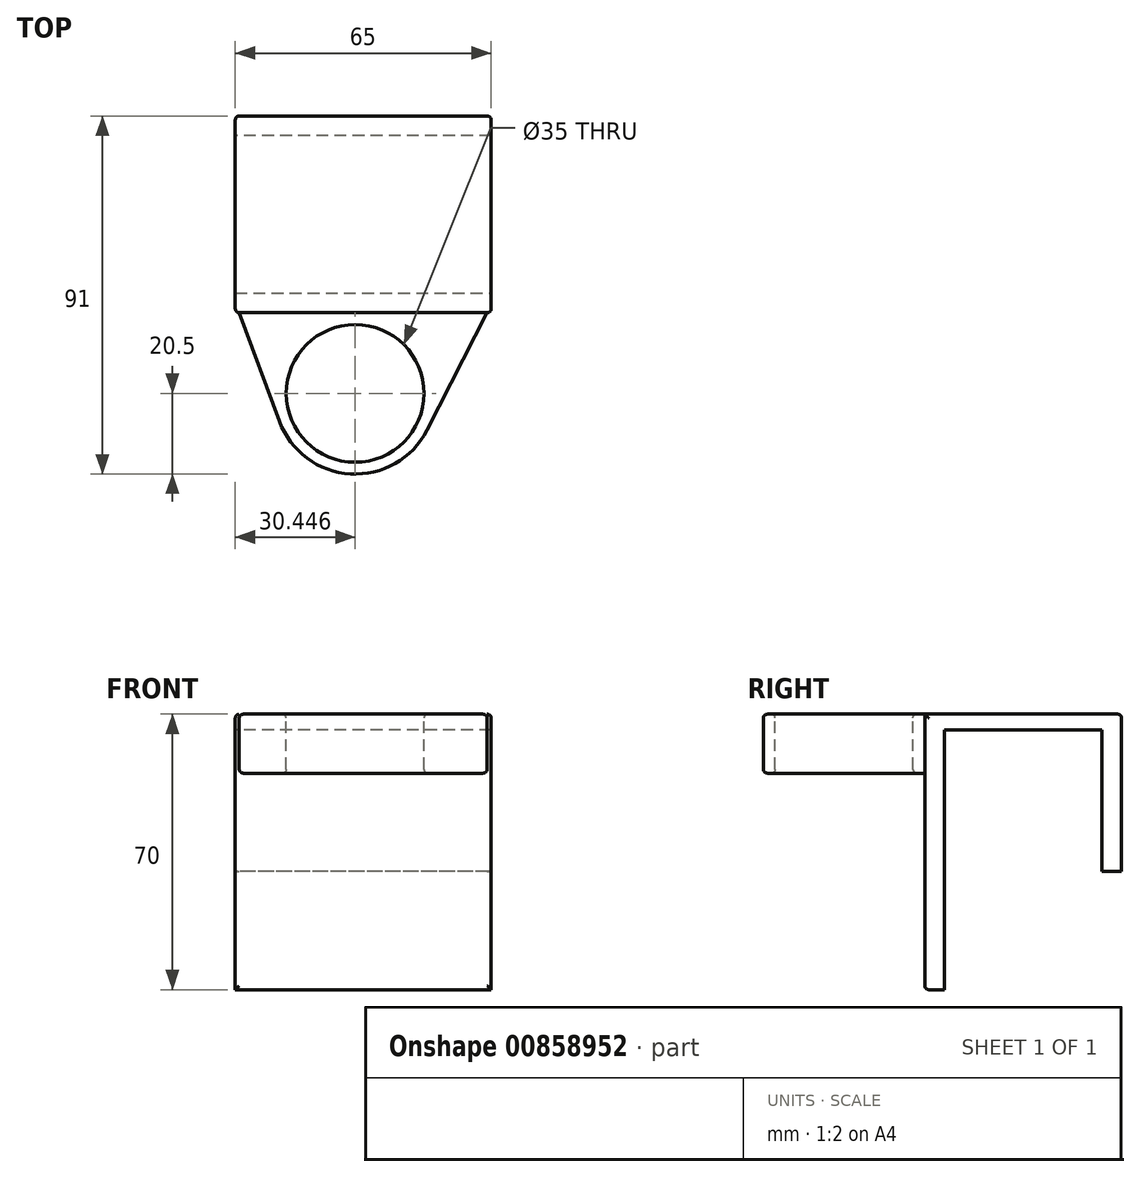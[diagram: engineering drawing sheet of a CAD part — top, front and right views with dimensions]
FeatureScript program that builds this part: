
annotation { "Feature Type Name" : "Feature", "Feature Type Description" : "" }
export const myFeature = defineFeature(function(context is Context, id is Id, definition is map)
    precondition{}
    {
        {
            var Q0;
            Q0=qCreatedBy(makeId("Front.planeOp"),FACE);
            var sketch = newSketch(context, id + "F0", { "sketchPlane" : qUnion([Q0])});
            skLineSegment(sketch, "E0.bottom", {"start": v(-49.34, 35.14) * mm, "end": v(15.66, 35.14) * mm});
            skLineSegment(sketch, "E0.top", {"start": v(-49.34, -34.86) * mm, "end": v(15.66, -34.86) * mm});
            skLineSegment(sketch, "E0.left", {"start": v(-49.34, 35.14) * mm, "end": v(-49.34, -34.86) * mm});
            skLineSegment(sketch, "E0.right", {"start": v(15.66, 35.14) * mm, "end": v(15.66, -34.86) * mm});
            skSolve(sketch);
        }
        {
            var Q0;
            Q0 = qSketchRegion(id + "F0", true);
            extrude(context, id + "F1", {"entities" : qUnion([Q0]), "oppositeDirection" : true, "depth" : 50 * mm, "offsetDistance" : 25.4 * mm});
        }
        {
            var Q0;
            Q0=makeQuery(id+"F1.opExtrude","SWEPT_FACE",FACE,{"disambiguationData":[OSD([sQuery(id+"F0.wireOp",EDGE,"E0.top")])]});
            var sketch = newSketch(context, id + "F2", { "sketchPlane" : qUnion([Q0])});
            skLineSegment(sketch, "E1.bottom", {"start": v(-49.34, -5) * mm, "end": v(15.66, -5) * mm});
            skLineSegment(sketch, "E1.top", {"start": v(-49.34, -45) * mm, "end": v(15.66, -45) * mm});
            skLineSegment(sketch, "E1.left", {"start": v(-49.34, -5) * mm, "end": v(-49.34, -45) * mm});
            skLineSegment(sketch, "E1.right", {"start": v(15.66, -5) * mm, "end": v(15.66, -45) * mm});
            skLineSegment(sketch, "E2.bottom", {"start": v(-16.84, 0) * mm, "end": v(-16.84, 0) * mm});
            skLineSegment(sketch, "E2.top", {"start": v(-16.84, -5) * mm, "end": v(-16.84, -5) * mm});
            skLineSegment(sketch, "E2.left", {"start": v(-16.84, 0) * mm, "end": v(-16.84, -5) * mm, "construction": true});
            skLineSegment(sketch, "E2.right", {"start": v(-16.84, 0) * mm, "end": v(-16.84, -5) * mm, "construction": true});
            skLineSegment(sketch, "E3.bottom", {"start": v(-16.84, -45) * mm, "end": v(-16.84, -45) * mm});
            skLineSegment(sketch, "E3.top", {"start": v(-16.84, -50) * mm, "end": v(-16.84, -50) * mm});
            skLineSegment(sketch, "E3.left", {"start": v(-16.84, -45) * mm, "end": v(-16.84, -50) * mm, "construction": true});
            skLineSegment(sketch, "E3.right", {"start": v(-16.84, -45) * mm, "end": v(-16.84, -50) * mm, "construction": true});
            skSolve(sketch);
        }
        {
            var Q0;
            Q0=makeQuery(id+"F2.imprint","IMPRINT",FACE,{"disambiguationData":[TD([[makeQuery(id+"F2.imprint","IMPRINT",EDGE,{"derivedFrom":sQuery(id+"F2.wireOp",EDGE,"E1.bottom")}),-1.0]])]});
            extrude(context, id + "F3", {"entities" : qUnion([Q0]), "operationType" : NewBodyOperationType.REMOVE, "endBound" : BoundingType.UP_TO_NEXT, "oppositeDirection" : true, "depth" : 25 * mm, "hasOffset" : true, "offsetDistance" : 4 * mm});
        }
        {
            var Q0;
            {var subQ2=sQuery(id+"F0.wireOp",EDGE,"E0.top");Q0=makeQuery(id+"F3.boolean.opBoolean","SPLIT",FACE,{"disambiguationData":[TD([makeQuery(id+"F3.opExtrude","SWEPT_FACE",FACE,{"disambiguationData":[OSD([sQuery(id+"F2.wireOp",EDGE,"E1.top")])]})])],"derivedFrom":makeQuery(id+"F1.opExtrude","SWEPT_FACE",FACE,{"disambiguationData":[OSD([subQ2])]})});}
            extrude(context, id + "F4", {"entities" : qUnion([Q0]), "operationType" : NewBodyOperationType.REMOVE, "endBound" : BoundingType.UP_TO_NEXT, "oppositeDirection" : true, "depth" : 25 * mm, "hasOffset" : true, "offsetDistance" : 40 * mm});
        }
        {
            var Q0;
            Q0=makeQuery(id+"F1.opExtrude","SWEPT_FACE",FACE,{"disambiguationData":[OSD([sQuery(id+"F0.wireOp",EDGE,"E0.bottom")])]});
            var sketch = newSketch(context, id + "F5", { "sketchPlane" : qUnion([Q0])});
            skCircle(sketch, "E4", {"center": v(-18.9, -20.5) * mm, "radius": 17.5 * mm});
            skCircle(sketch, "E5", {"center": v(-18.9, -20.5) * mm, "radius": 20.5 * mm});
            skLineSegment(sketch, "E6", {"start": v(-38.12, -27.61) * mm, "end": v(-48.34, 0) * mm});
            skLineSegment(sketch, "E7", {"start": v(14.66, 0) * mm, "end": v(-0.65, -29.86) * mm});
            skLineSegment(sketch, "E8", {"start": v(-48.34, 50) * mm, "end": v(-48.34, 0) * mm, "construction": true});
            skLineSegment(sketch, "E9", {"start": v(14.66, 50) * mm, "end": v(14.66, 0) * mm, "construction": true});
            skSolve(sketch);
        }
        {
            var Q0;
            Q0=makeQuery(id+"F5.imprint","IMPRINT",FACE,{"disambiguationData":[TD([[makeQuery(id+"F5.imprint","IMPRINT",EDGE,{"derivedFrom":sQuery(id+"F5.wireOp",EDGE,"E4")}),1.0]])]});
            extrude(context, id + "F6", {"entities" : qUnion([Q0]), "operationType" : NewBodyOperationType.REMOVE, "oppositeDirection" : true, "depth" : 25 * mm, "offsetDistance" : 25 * mm});
        }
        {
            var Q0;
            {var subQ0=sQuery(id+"F5.wireOp",EDGE,"E6");Q0=makeQuery(id+"F5.imprint","IMPRINT",FACE,{"disambiguationData":[TD([[makeQuery(id+"F5.imprint","IMPRINT",EDGE,{"derivedFrom":subQ0}),-1.0]])]});}
            var Q1;
            {var subQ0=sQuery(id+"F5.wireOp",EDGE,"E7");Q1=makeQuery(id+"F5.imprint","IMPRINT",FACE,{"disambiguationData":[TD([[makeQuery(id+"F5.imprint","IMPRINT",EDGE,{"derivedFrom":subQ0}),-1.0]])]});}
            var Q2;
            Q2=makeQuery(id+"F5.imprint","IMPRINT",FACE,{"disambiguationData":[TD([[makeQuery(id+"F5.imprint","IMPRINT",EDGE,{"derivedFrom":sQuery(id+"F5.wireOp",EDGE,"E4")}),-1.0]])]});
            extrude(context, id + "F7", {"entities" : qUnion([Q0, Q1, Q2]), "oppositeDirection" : true, "depth" : 15 * mm, "offsetDistance" : 25 * mm});
        }
        {
            var Q0;
            Q0=makeQuery(id+"F7.opExtrude","CAP_EDGE",EDGE,{"disambiguationData":[OSD([sQuery(id+"F5.wireOp",EDGE,"E6")])],"isStart":true});
            var Q1;
            Q1=makeQuery(id+"F7.opExtrude","CAP_EDGE",EDGE,{"disambiguationData":[OSD([sQuery(id+"F5.wireOp",EDGE,"E4")])],"isStart":true});
            var Q2;
            Q2=makeQuery(id+"F7.opExtrude","CAP_EDGE",EDGE,{"disambiguationData":[OSD([sQuery(id+"F5.wireOp",EDGE,"E6")])],"isStart":false});
            var Q3;
            Q3=makeQuery(id+"F1.opExtrude","SWEPT_EDGE",EDGE,{"disambiguationData":[OSD([sQuery(id+"F0.wireOp",EDGE,"E0.bottom"),sQuery(id+"F0.wireOp",EDGE,"E0.right")])]});
            var Q4;
            Q4=makeQuery(id+"F1.opExtrude","SWEPT_EDGE",EDGE,{"disambiguationData":[OSD([sQuery(id+"F0.wireOp",EDGE,"E0.bottom"),sQuery(id+"F0.wireOp",EDGE,"E0.left")])]});
            var Q5;
            Q5=makeQuery(id+"F4.boolean.opBoolean","COPY",EDGE,{"derivedFrom":makeQuery(id+"F4.opExtrude","CAP_EDGE",EDGE,{"disambiguationData":[OSD([sQuery(id+"F0.wireOp",EDGE,"E0.top")])],"isStart":false})});
            var Q6;
            Q6=makeQuery(id+"F1.opExtrude","CAP_EDGE",EDGE,{"disambiguationData":[OSD([sQuery(id+"F0.wireOp",EDGE,"E0.right")])],"isStart":false});
            var Q7;
            Q7=makeQuery(id+"F1.opExtrude","CAP_EDGE",EDGE,{"disambiguationData":[OSD([sQuery(id+"F0.wireOp",EDGE,"E0.left")])],"isStart":false});
            var Q8;
            Q8=makeQuery(id+"F1.opExtrude","CAP_EDGE",EDGE,{"disambiguationData":[OSD([sQuery(id+"F0.wireOp",EDGE,"E0.top")])],"isStart":true});
            var Q9;
            Q9=makeQuery(id+"F7.opExtrude","CAP_EDGE",EDGE,{"disambiguationData":[OSD([sQuery(id+"F5.wireOp",EDGE,"E4")])],"isStart":false});
            var Q10;
            Q10=makeQuery(id+"F1.opExtrude","CAP_EDGE",EDGE,{"disambiguationData":[OSD([sQuery(id+"F0.wireOp",EDGE,"E0.bottom")])],"isStart":false});
            var Q11;
            Q11=makeQuery(id+"F1.opExtrude","CAP_EDGE",EDGE,{"disambiguationData":[OSD([sQuery(id+"F0.wireOp",EDGE,"E0.left")])],"isStart":true});
            var Q12;
            Q12=makeQuery(id+"F1.opExtrude","CAP_EDGE",EDGE,{"disambiguationData":[OSD([sQuery(id+"F0.wireOp",EDGE,"E0.right")])],"isStart":true});
            fillet(context, id + "F8", {"entities" : qUnion([Q0, Q1, Q2, Q3, Q4, Q5, Q6, Q7, Q8, Q9, Q10, Q11, Q12]), "radius" : 1 * mm, "tangentPropagation" : true, "allowEdgeOverflow" : false});
        }
    });
